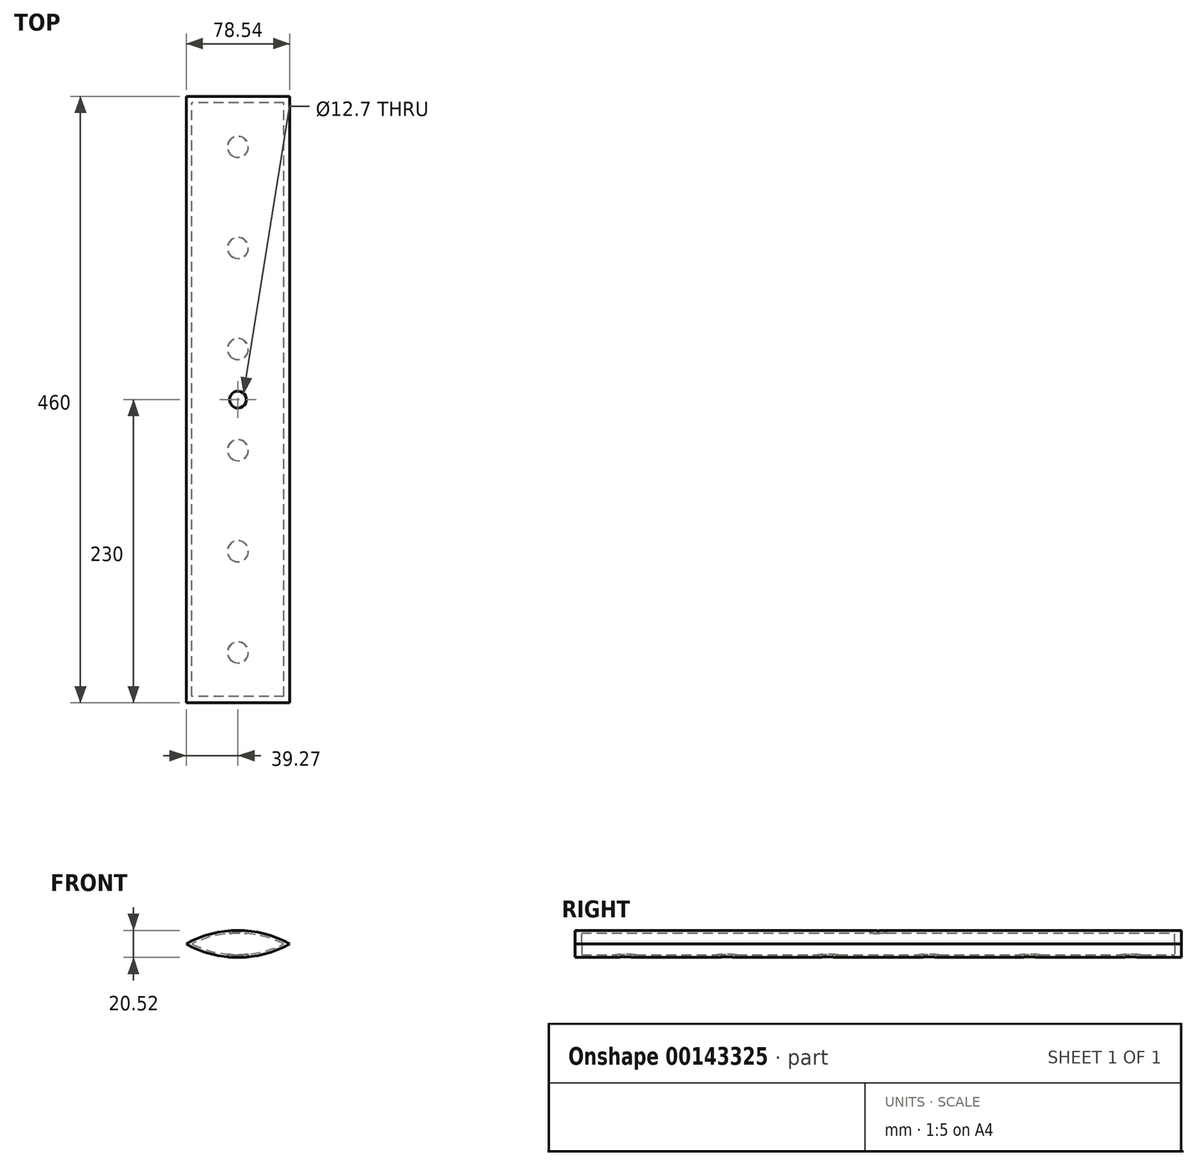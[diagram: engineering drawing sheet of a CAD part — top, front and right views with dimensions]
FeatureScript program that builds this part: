
annotation { "Feature Type Name" : "Feature", "Feature Type Description" : "" }
export const myFeature = defineFeature(function(context is Context, id is Id, definition is map)
    precondition{}
    {
        {
            var Q0;
            Q0=qCreatedBy(makeId("Front.planeOp"),FACE);
            var sketch = newSketch(context, id + "F0", { "sketchPlane" : qUnion([Q0])});
            skArc(sketch, "E0", {"start": v(-35, 0) * mm, "mid": v(0, -8.26) * mm, "end": v(35, 0) * mm});
            skArc(sketch, "E1", {"start": v(-35, 0) * mm, "mid": v(0, 8.26) * mm, "end": v(35, 0) * mm});
            skArc(sketch, "E2.0", {"start": v(-39.27, 0) * mm, "mid": v(0, 10.26) * mm, "end": v(39.27, 0) * mm});
            skArc(sketch, "E2.1", {"start": v(-39.27, 0) * mm, "mid": v(0, -10.26) * mm, "end": v(39.27, 0) * mm});
            skSolve(sketch);
        }
        {
            var Q0;
            Q0 = qSketchRegion(id + "F0", true);
            extrude(context, id + "F1", {"entities" : qUnion([Q0]), "endBound" : BoundingType.SYMMETRIC, "depth" : 460 * mm});
        }
        {
            var Q0;
            Q0=qCreatedBy(makeId("Top.planeOp"),FACE);
            var sketch = newSketch(context, id + "F2", { "sketchPlane" : qUnion([Q0])});
            skLineSegment(sketch, "E3", {"start": v(0, 230) * mm, "end": v(0, 191.67) * mm});
            skLineSegment(sketch, "E4", {"start": v(0, 191.67) * mm, "end": v(0, 115) * mm});
            skLineSegment(sketch, "E5", {"start": v(0, 38.33) * mm, "end": v(0, 115) * mm});
            skLineSegment(sketch, "E6", {"start": v(0, 38.33) * mm, "end": v(0, -38.33) * mm});
            skLineSegment(sketch, "E7", {"start": v(0, -38.33) * mm, "end": v(0, -115) * mm});
            skLineSegment(sketch, "E8", {"start": v(0, -191.67) * mm, "end": v(0, -115) * mm});
            skCircle(sketch, "E9", {"center": v(0, -191.67) * mm, "radius": 7.5 * mm});
            skCircle(sketch, "E10", {"center": v(0, -115) * mm, "radius": 7.5 * mm});
            skCircle(sketch, "E11", {"center": v(0, -38.33) * mm, "radius": 7.5 * mm});
            skCircle(sketch, "E12", {"center": v(0, 38.33) * mm, "radius": 7.5 * mm});
            skCircle(sketch, "E13", {"center": v(0, 115) * mm, "radius": 7.5 * mm});
            skCircle(sketch, "E14", {"center": v(0, 191.67) * mm, "radius": 7.5 * mm});
            skSolve(sketch);
        }
        {
            var Q0;
            Q0 = qSketchRegion(id + "F2", true);
            extrude(context, id + "F3", {"entities" : qUnion([Q0]), "operationType" : NewBodyOperationType.REMOVE, "oppositeDirection" : true, "depth" : 25 * mm, "hasDraft" : true, "draftAngle" : 3 * degree});
        }
        {
            var Q0;
            Q0=qCreatedBy(makeId("Front.planeOp"),FACE);
            var sketch = newSketch(context, id + "F4", { "sketchPlane" : qUnion([Q0])});
            skArc(sketch, "E15", {"start": v(-35, 0) * mm, "mid": v(0, -8.26) * mm, "end": v(35, 0) * mm});
            skArc(sketch, "E16", {"start": v(-35, 0) * mm, "mid": v(0, 8.26) * mm, "end": v(35, 0) * mm});
            skLineSegment(sketch, "E17", {"start": v(-35, 0) * mm, "end": v(35, 0) * mm});
            skSolve(sketch);
        }
        {
            var Q0;
            Q0 = qSketchRegion(id + "F4", true);
            extrude(context, id + "F5", {"entities" : qUnion([Q0]), "operationType" : NewBodyOperationType.ADD, "endBound" : BoundingType.SYMMETRIC, "depth" : 460 * mm});
        }
        {
            var Q0;
            Q0 = qSketchRegion(id + "F4", true);
            extrude(context, id + "F6", {"entities" : qUnion([Q0]), "operationType" : NewBodyOperationType.REMOVE, "endBound" : BoundingType.SYMMETRIC, "depth" : 450 * mm});
        }
        {
            var Q0;
            Q0=qCreatedBy(makeId("Top.planeOp"),FACE);
            var sketch = newSketch(context, id + "F7", { "sketchPlane" : qUnion([Q0])});
            skCircle(sketch, "E18", {"center": v(0, 0) * mm, "radius": 6.35 * mm});
            skSolve(sketch);
        }
        {
            var Q0;
            Q0 = qSketchRegion(id + "F7", true);
            extrude(context, id + "F8", {"entities" : qUnion([Q0]), "operationType" : NewBodyOperationType.REMOVE, "depth" : 25 * mm});
        }
    });
